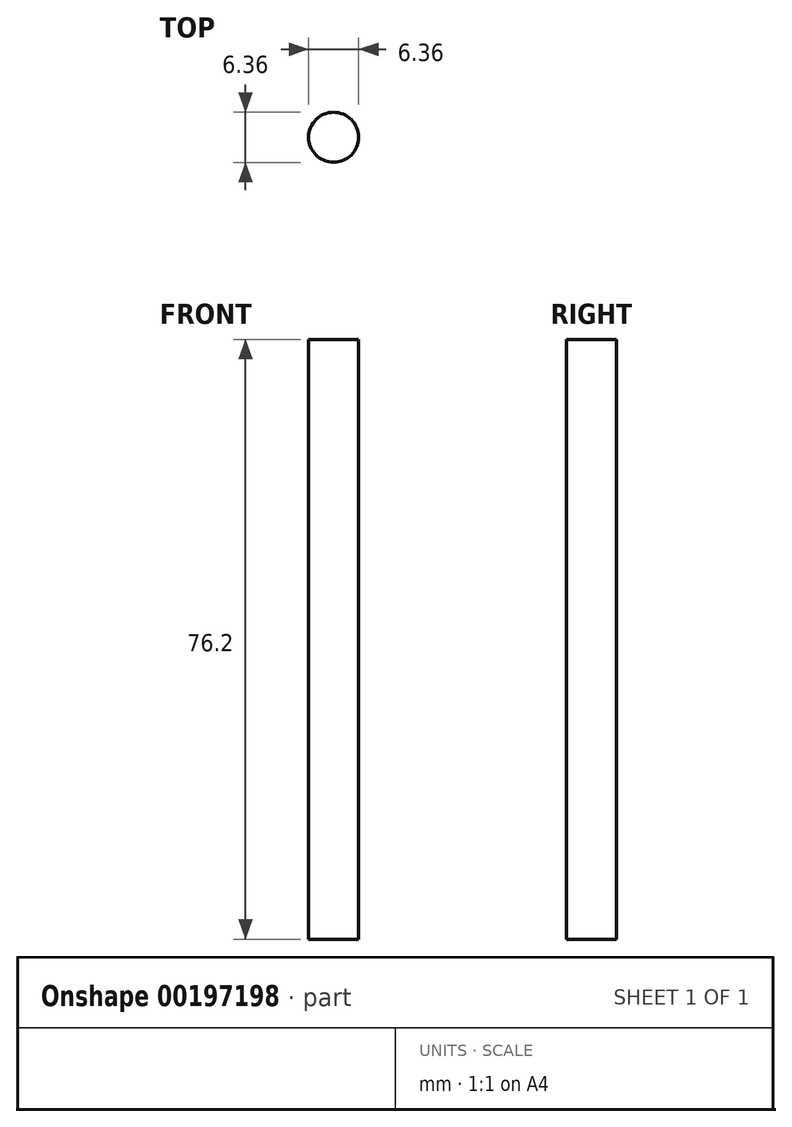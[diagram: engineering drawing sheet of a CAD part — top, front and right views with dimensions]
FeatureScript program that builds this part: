
annotation { "Feature Type Name" : "Feature", "Feature Type Description" : "" }
export const myFeature = defineFeature(function(context is Context, id is Id, definition is map)
    precondition{}
    {
        {
            var Q0;
            Q0=qCreatedBy(makeId("Top.planeOp"),FACE);
            var sketch = newSketch(context, id + "F0", { "sketchPlane" : qUnion([Q0])});
            skCircle(sketch, "E0", {"center": v(0, 0) * mm, "radius": 3.18 * mm});
            skSolve(sketch);
        }
        {
            var Q0;
            Q0 = qSketchRegion(id + "F0", true);
            extrude(context, id + "F1", {"entities" : qUnion([Q0]), "depth" : 76.2 * mm});
        }
    });
